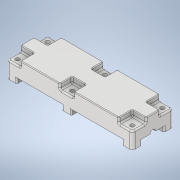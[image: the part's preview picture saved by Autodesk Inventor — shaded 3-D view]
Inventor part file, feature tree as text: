
AUTODESK INVENTOR PART (.ipt)
format: ipt  version: 2021 (Build 250183000, 183)  size: 861,184 bytes
history: native  units: mm
features: sketch x22, extrude x21, projected_geometry x9, fillet x3, other x1, mirror x1, boolean_combine x1
ambient origin geometry x8: Origin, YZ Plane, XZ Plane, XY Plane, X Axis, Y Axis, Z Axis, Center Point
bodies: Volumenkörper1 (feature_tree), Solid2 (feature_tree), Solid3 (feature_tree)
feature tree (58):
  extrude  "Extrusion1"  Depth=11.0mm
  other  "Spirale1"
  mirror  "Spiegeln1"
  extrude  "Extrusion5"  Depth=4.0mm
  extrude  "Extrusion6"  Depth=1.0mm
  boolean_combine  "Combine1"
  extrude  "Extrusion7"  Depth=10.0mm TaperAngle=0.0deg
  extrude  "Extrusion8"  Depth=7.0mm TaperAngle=0.0deg
  extrude  "Extrusion9"  Depth=24.0mm
  extrude  "Extrusion10"  Depth=12.0mm TaperAngle=0.0deg
  extrude  "Extrusion11"  Depth=4.0mm
  extrude  "Extrusion13"  Depth=10.0mm
  fillet  "Fillet2"  Radius=10.0mm
  fillet  "Fillet3"  Radius=77.15mm
  fillet  "Fillet4"  Radius=30.0mm
  extrude  "Extrusion14"  Depth=4.0mm
  extrude  "Extrusion15"  Depth=10.0mm TaperAngle=0.0deg
  extrude  "Extrusion16"  Depth=3.0mm
  extrude  "Extrusion17"  Depth=4.0mm
  extrude  "Extrusion19"  Depth=4.0mm
  extrude  "Extrusion20"  Depth=6.9mm
  extrude  "Extrusion21"  Depth=7.0mm
  extrude  "Extrusion22"  Depth=6.9mm
  extrude  "Extrusion23"  Depth=10.0mm
  extrude  "Extrusion25"  Depth=10.0mm
  extrude  "Extrusion26"  Depth=10.0mm
  extrude  "Extrusion27"  Depth=10.0mm
  sketch  "Skizze1"  dims[d0=6.0mm d1=11.0mm]
  sketch  "Skizze3"  dims[d2=36.0mm d3=0.0mm]
  projected_geometry  "Projizierte Kontur2"
  sketch  "Sketch7"  dims[d8=7.0mm d9=24.5mm d10=10.0mm d11=0.0mm d12=90.0deg d13=90.0deg d14=0.0mm d15=0.0mm d16=4.0mm]
  sketch  "Sketch8"  dims[d17=13.962634mm d18=1.0mm]
  sketch  "Sketch9"  dims[d19=0.1mm d32=10.0mm d33=0.0mm]
  projected_geometry  "Projected Loop4"
  sketch  "Sketch10"  dims[d34=7.0mm d35=100.0mm d36=0.0mm]
  sketch  "Sketch11"  dims[d37=82.0mm d38=0.0mm d39=24.0mm]
  projected_geometry  "Projected Loop5"
  projected_geometry  "Projected Loop6"
  sketch  "Sketch12"  dims[d40=30.0mm d41=12.0mm d42=0.0mm]
  sketch  "Sketch13"  dims[d43=3.0mm d44=4.0mm]
  projected_geometry  "Projected Loop7"
  projected_geometry  "Projected Loop8"
  sketch  "Sketch15"  dims[d45=4.0mm d46=20.0mm d48=22.0mm d49=20.0mm d51=84.0mm d54=10.0mm d55=0.0mm d56=77.15mm d57=30.0mm]
  sketch  "Sketch16"  dims[d62=4.0mm d63=0.0mm d64=6.0mm]
  projected_geometry  "Projected Loop10"
  sketch  "Sketch17"  dims[d65=10.0mm d66=0.0mm d67=10.0mm d68=0.0mm]
  projected_geometry  "Projected Loop11"
  projected_geometry  "Projected Loop12"
  sketch  "Sketch18"  dims[d76=3.0mm d77=3.0mm]
  sketch  "Sketch19"  dims[d78=4.0mm d79=48.0mm]
  sketch  "Sketch21"  dims[d80=46.0mm d81=4.0mm]
  sketch  "Sketch22"  dims[d85=7.0mm d86=6.9mm]
  sketch  "Sketch23"  dims[d87=3.5mm d88=7.0mm]
  sketch  "Sketch24"  dims[d89=6.9mm d90=3.5mm]
  sketch  "Sketch25"  dims[d91=10.0mm d92=10.0mm]
  sketch  "Sketch27"  dims[d93=10.0mm d94=10.0mm]
  sketch  "Sketch28"  dims[d95=10.0mm d96=10.0mm]
  sketch  "Sketch29"  dims[d97=10.0mm d98=10.0mm d99=10.0mm d100=10.0mm d101=10.0mm d102=10.0mm d103=4.0mm d104=0.0mm d105=1.0mm d106=1.0mm d107=2.0mm d108=0.5mm d109=6.5mm d110=2.1mm d111=0.0mm d112=6.5mm d113=2.1mm d114=0.0mm d115=180.0deg d116=6.9mm d117=6.9mm d118=6.9mm d119=6.9mm d120=12.0mm d121=0.2mm d122=0.0mm d123=15.0mm d124=0.2mm d125=0.0mm d126=7.9mm d127=0.0mm d128=7.9mm d129=0.0mm d132=1.9mm d133=0.0mm d134=5.1mm d135=5.0mm d136=0.0mm d137=6.6mm d138=1.9mm d139=0.0mm d140=4.1mm d141=3.1mm d142=0.0mm d143=6.6mm d144=3.1mm d145=0.0mm d149=6.6mm d150=0.2mm d151=0.0mm d152=5.1mm d153=7.9mm d154=0.0mm d155=2.0mm d156=0.0mm d157=0.5mm d158=0.872665mm]
